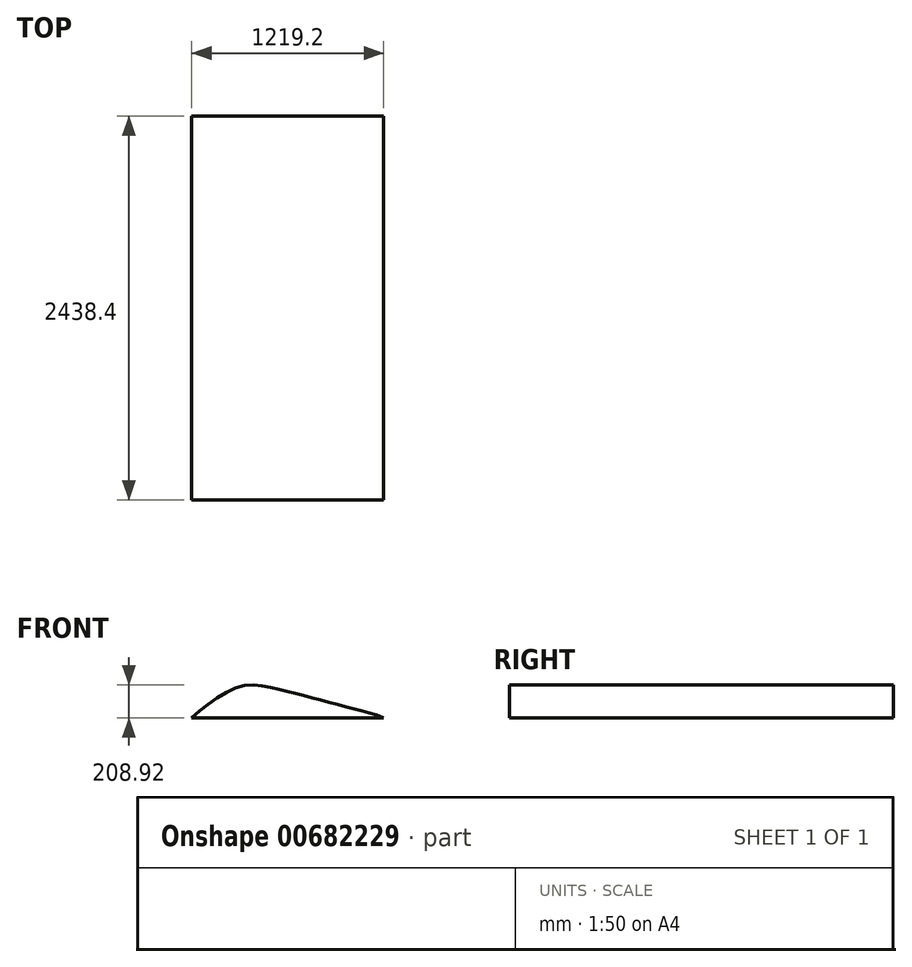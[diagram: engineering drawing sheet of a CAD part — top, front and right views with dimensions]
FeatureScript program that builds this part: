
annotation { "Feature Type Name" : "Feature", "Feature Type Description" : "" }
export const myFeature = defineFeature(function(context is Context, id is Id, definition is map)
    precondition{}
    {
        {
            var Q0;
            Q0=qCreatedBy(makeId("Front.planeOp"),FACE);
            var sketch = newSketch(context, id + "F0", { "sketchPlane" : qUnion([Q0])});
            skLineSegment(sketch, "E0", {"start": v(-858.6, 0) * mm, "end": v(360.6, 0) * mm});
            skFitSpline(sketch, "E1", {"points": [v(-858.6, 0) * mm, v(-552.64, 198.31) * mm, v(-306.04, 181.3) * mm, v(-72.2, 121.78) * mm, v(170.15, 58) * mm, v(360.6, 0) * mm], "startDerivative": vector(1098.41, 944.93) * mm, "endDerivative": vector(1058.02, -439.1) * mm});
            skSolve(sketch);
        }
        {
            var Q0;
            Q0 = qSketchRegion(id + "F0", true);
            extrude(context, id + "F1", {"entities" : qUnion([Q0]), "depth" : 2438.4 * mm, "offsetDistance" : 25.4 * mm});
        }
    });
